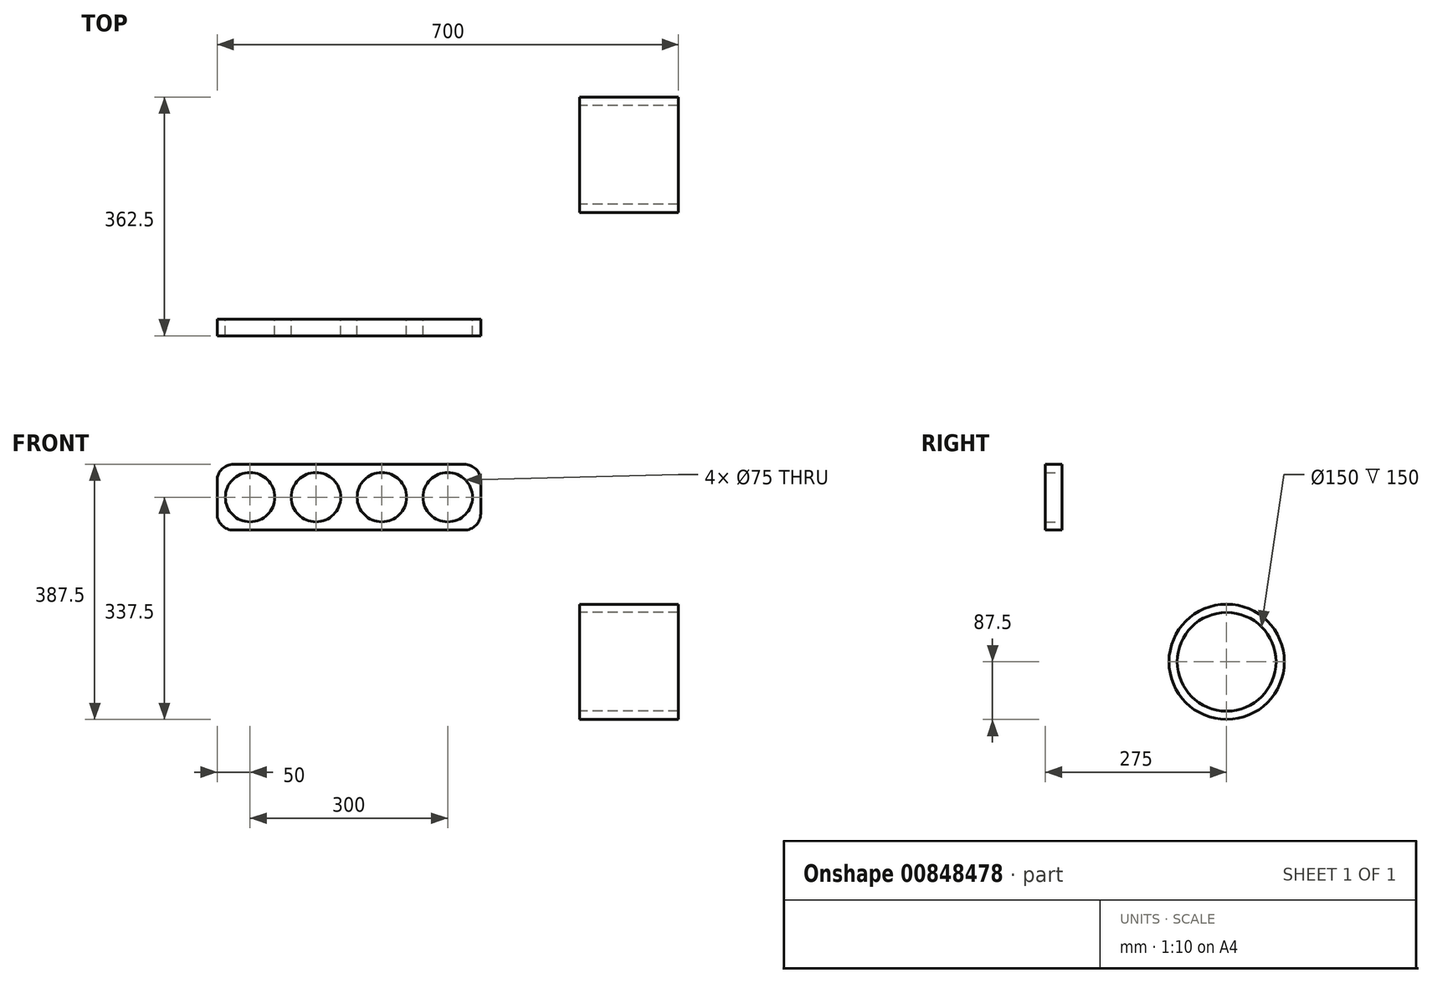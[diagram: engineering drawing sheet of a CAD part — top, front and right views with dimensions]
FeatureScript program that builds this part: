
annotation { "Feature Type Name" : "Feature", "Feature Type Description" : "" }
export const myFeature = defineFeature(function(context is Context, id is Id, definition is map)
    precondition{}
    {
        {
            var Q0;
            Q0=qCreatedBy(makeId("Front.planeOp"),FACE);
            var sketch = newSketch(context, id + "F0", { "sketchPlane" : qUnion([Q0])});
            skCircle(sketch, "E0", {"center": v(0, 0) * mm, "radius": 37.5 * mm});
            skCircle(sketch, "E1.1.0.0", {"center": v(100, 0) * mm, "radius": 37.5 * mm});
            skCircle(sketch, "E1.2.0.0", {"center": v(200, 0) * mm, "radius": 37.5 * mm});
            skLineSegment(sketch, "E1.direction1", {"start": v(0, 0) * mm, "end": v(100, 0) * mm, "construction": true});
            skCircle(sketch, "E2.1.0.0", {"center": v(-100, 0) * mm, "radius": 37.5 * mm});
            skLineSegment(sketch, "E2.direction1", {"start": v(0, 0) * mm, "end": v(-100, 0) * mm, "construction": true});
            skLineSegment(sketch, "E3.bottom", {"start": v(225, 50) * mm, "end": v(-125, 50) * mm});
            skLineSegment(sketch, "E3.top", {"start": v(225, -50) * mm, "end": v(-125, -50) * mm});
            skLineSegment(sketch, "E3.left", {"start": v(250, 25) * mm, "end": v(250, -25) * mm});
            skLineSegment(sketch, "E3.right", {"start": v(-150, 25) * mm, "end": v(-150, -25) * mm});
            skPoint(sketch, "E4.visualSharp", {"position": v(250, 50) * mm});
            skArc(sketch, "E4.filletArc", {"start": v(250, 25) * mm, "mid": v(242.68, 42.68) * mm, "end": v(225, 50) * mm});
            skPoint(sketch, "E5.visualSharp", {"position": v(250, -50) * mm});
            skArc(sketch, "E5.filletArc", {"start": v(225, -50) * mm, "mid": v(242.68, -42.68) * mm, "end": v(250, -25) * mm});
            skPoint(sketch, "E6.visualSharp", {"position": v(-150, -50) * mm});
            skArc(sketch, "E6.filletArc", {"start": v(-150, -25) * mm, "mid": v(-142.68, -42.68) * mm, "end": v(-125, -50) * mm});
            skPoint(sketch, "E7.visualSharp", {"position": v(-150, 50) * mm});
            skArc(sketch, "E7.filletArc", {"start": v(-125, 50) * mm, "mid": v(-142.68, 42.68) * mm, "end": v(-150, 25) * mm});
            skSolve(sketch);
        }
        {
            var Q0;
            Q0=makeQuery(id+"F0.imprint","IMPRINT",FACE,{"disambiguationData":[TD([[makeQuery(id+"F0.imprint","IMPRINT",EDGE,{"derivedFrom":sQuery(id+"F0.wireOp",EDGE,"E0")}),-1.0]])]});
            extrude(context, id + "F1", {"entities" : qUnion([Q0]), "depth" : 25 * mm, "offsetDistance" : 25 * mm});
        }
        {
            var Q0;
            Q0=qCreatedBy(makeId("Right.planeOp"),FACE);
            cPlane(context, id + "F2", {"entities" : qUnion([Q0]), "cplaneType" : CPlaneType.OFFSET, "offset" : 400 * mm, "width" : 150 * mm, "height" : 150 * mm});
        }
        {
            var Q0;
            Q0=qCreatedBy(id+"F2.planeOp",FACE);
            var sketch = newSketch(context, id + "F3", { "sketchPlane" : qUnion([Q0])});
            skCircle(sketch, "E8", {"center": v(250, -250) * mm, "radius": 75 * mm});
            skCircle(sketch, "E9", {"center": v(250, -250) * mm, "radius": 87.5 * mm});
            skPoint(sketch, "E10", {"position": v(212.5, -212.5) * mm});
            skPoint(sketch, "E11", {"position": v(287.5, -212.5) * mm});
            skPoint(sketch, "E12", {"position": v(287.5, -287.5) * mm});
            skPoint(sketch, "E13", {"position": v(212.5, -287.5) * mm});
            skLineSegment(sketch, "E14", {"start": v(250, -200.3) * mm, "end": v(250, -315.96) * mm, "construction": true});
            skLineSegment(sketch, "E15", {"start": v(203.97, -250) * mm, "end": v(297.6, -250) * mm, "construction": true});
            skSolve(sketch);
        }
        {
            var Q0;
            Q0=makeQuery(id+"F3.imprint","IMPRINT",FACE,{"disambiguationData":[TD([[makeQuery(id+"F3.imprint","IMPRINT",EDGE,{"derivedFrom":sQuery(id+"F3.wireOp",EDGE,"E8")}),-1.0]])]});
            extrude(context, id + "F4", {"entities" : qUnion([Q0]), "depth" : 150 * mm, "offsetDistance" : 25 * mm});
        }
        {
            var Q0;
            Q0=makeQuery(id+"F1.opExtrude","CAP_FACE",FACE,{"disambiguationData":[OSD([sQuery(id+"F0.wireOp",EDGE,"E0"),sQuery(id+"F0.wireOp",EDGE,"E1.1.0.0"),sQuery(id+"F0.wireOp",EDGE,"E1.2.0.0"),sQuery(id+"F0.wireOp",EDGE,"E2.1.0.0"),sQuery(id+"F0.wireOp",EDGE,"E2.2.0.0"),sQuery(id+"F0.wireOp",EDGE,"E3.bottom"),sQuery(id+"F0.wireOp",EDGE,"E3.top"),sQuery(id+"F0.wireOp",EDGE,"E3.left"),sQuery(id+"F0.wireOp",EDGE,"E3.right"),sQuery(id+"F0.wireOp",EDGE,"E4.filletArc"),sQuery(id+"F0.wireOp",EDGE,"E5.filletArc"),sQuery(id+"F0.wireOp",EDGE,"E6.filletArc"),sQuery(id+"F0.wireOp",EDGE,"E7.filletArc")])],"isStart":true});
            var sketch = newSketch(context, id + "F5", { "sketchPlane" : qUnion([Q0])});
            skSolve(sketch);
        }
        {
            var Q0;
            Q0=qCreatedBy(makeId("Top.planeOp"),FACE);
            var sketch = newSketch(context, id + "F6", { "sketchPlane" : qUnion([Q0])});
            skLineSegment(sketch, "E16", {"start": v(0, 0) * mm, "end": v(0, 100) * mm});
            skSolve(sketch);
        }
        {
            var Q0;
            Q0=sQuery(id+"F3.wireOp",VERTEX,"E13");
            var Q1;
            Q1=sQuery(id+"F6.wireOp",VERTEX,"E16.start");
            var Q2;
            Q2=sQuery(id+"F6.wireOp",VERTEX,"E16.end");
            cPlane(context, id + "F7", {"entities" : qUnion([Q0, Q1, Q2]), "cplaneType" : CPlaneType.THREE_POINT, "offset" : 25 * mm, "width" : 150 * mm, "height" : 150 * mm});
        }
        {
            var Q0;
            Q0=qCreatedBy(id+"F7.planeOp",FACE);
            var sketch = newSketch(context, id + "F8", { "sketchPlane" : qUnion([Q0])});
            skFitSpline(sketch, "E17", {"points": [v(0, 0) * mm, v(20.62, 108.28) * mm, v(50.2, 149.12) * mm, v(129.88, 178.68) * mm, v(492.6, 212.5) * mm], "startDerivative": vector(3.3, 675.9) * mm, "endDerivative": vector(691.04, -30.42) * mm});
            skSolve(sketch);
        }
        {
            var Q0;
            Q0=makeQuery(id+"F5.imprint","IMPRINT",FACE,{"disambiguationData":[TD([[makeQuery(id+"F5.imprint","IMPRINT",EDGE,{"derivedFrom":makeQuery(id+"F1.opExtrude","CAP_EDGE",EDGE,{"disambiguationData":[OSD([sQuery(id+"F0.wireOp",EDGE,"E0")])],"isStart":true})}),-1.0]])]});
            var Q1;
            Q1=makeQuery(id+"F1.opExtrude","CAP_EDGE",EDGE,{"disambiguationData":[OSD([sQuery(id+"F0.wireOp",EDGE,"E0")])],"isStart":true});
            var Q2;
            Q2=sQuery(id+"F8.wireOp",EDGE,"E17");
            sweep(context, id + "F9", {"bodyType" : ToolBodyType.SURFACE, "operationType" : NewBodyOperationType.ADD, "profiles" : qUnion([Q0]), "surfaceProfiles" : qUnion([Q1]), "path" : qUnion([Q2])});
        }
        {
            var Q0;
            Q0=qCreatedBy(makeId("Top.planeOp"),FACE);
            var sketch = newSketch(context, id + "F10", { "sketchPlane" : qUnion([Q0])});
            skLineSegment(sketch, "E18", {"start": v(-100, 0) * mm, "end": v(-100, 75.5) * mm, "construction": true});
            skLineSegment(sketch, "E19", {"start": v(100, 0) * mm, "end": v(100, 49.65) * mm, "construction": true});
            skLineSegment(sketch, "E20", {"start": v(200, 0) * mm, "end": v(200, 55.48) * mm, "construction": true});
            skSolve(sketch);
        }
        {
            var Q0;
            Q0=sQuery(id+"F10.wireOp",VERTEX,"E18.end");
            var Q1;
            Q1=sQuery(id+"F10.wireOp",VERTEX,"E18.start");
            var Q2;
            Q2=sQuery(id+"F3.wireOp",VERTEX,"E12");
            cPlane(context, id + "F11", {"entities" : qUnion([Q0, Q1, Q2]), "cplaneType" : CPlaneType.THREE_POINT, "offset" : 25 * mm, "width" : 150 * mm, "height" : 150 * mm});
        }
        {
            var Q0;
            Q0=qCreatedBy(id+"F11.planeOp",FACE);
            var sketch = newSketch(context, id + "F12", { "sketchPlane" : qUnion([Q0])});
            skLineSegment(sketch, "E21", {"start": v(-86.7, 0) * mm, "end": v(-86.7, -55.92) * mm});
            skFitSpline(sketch, "E22", {"points": [v(-86.7, -55.92) * mm, v(-26.3, -203.27) * mm, v(103.26, -277.05) * mm, v(490.07, -287.5) * mm], "startDerivative": vector(0, -587.12) * mm, "endDerivative": vector(806.55, 99.19) * mm});
            skSolve(sketch);
        }
        {
            var Q0;
            Q0=sQuery(id+"F10.wireOp",VERTEX,"E19.start");
            var Q1;
            Q1=sQuery(id+"F10.wireOp",VERTEX,"E19.end");
            var Q2;
            Q2=sQuery(id+"F3.wireOp",VERTEX,"E11");
            cPlane(context, id + "F13", {"entities" : qUnion([Q0, Q1, Q2]), "cplaneType" : CPlaneType.THREE_POINT, "offset" : 25 * mm, "width" : 150 * mm, "height" : 150 * mm});
        }
        {
            var Q0;
            Q0=qCreatedBy(id+"F13.planeOp",FACE);
            var sketch = newSketch(context, id + "F14", { "sketchPlane" : qUnion([Q0])});
            skLineSegment(sketch, "E23", {"start": v(81.6, 0) * mm, "end": v(81.6, 53.13) * mm});
            skFitSpline(sketch, "E24", {"points": [v(81.6, 53.13) * mm, v(81.6, 158.76) * mm, v(96.97, 231.36) * mm, v(152.02, 296.8) * mm, v(271.78, 321.94) * mm, v(449.24, 287.5) * mm], "startDerivative": vector(-38.65, 554.57) * mm, "endDerivative": vector(475.4, -114.78) * mm});
            skSolve(sketch);
        }
    });
